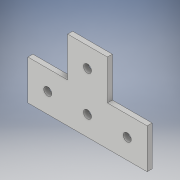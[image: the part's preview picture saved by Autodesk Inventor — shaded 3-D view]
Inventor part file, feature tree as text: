
AUTODESK INVENTOR PART (.ipt)
format: ipt  version: 2018 (Build 220112000, 112)  size: 110,592 bytes
history: native  units: in
note: dims shown in document units (in); Inventor stores cm internally (conversion verified against a paired STEP export)
features: extrude x1, sketch x1
ambient origin geometry x8: Origin, YZ Plane, XZ Plane, XY Plane, X Axis, Y Axis, Z Axis, Center Point
bodies: Solid1 (feature_tree)
feature tree (2):
  extrude  "Extrusion1"  Depth=1.0in
  sketch  "Sketch1"  dims[d0=1.0in d1=1.0in d2=1.0in d3=1.0in d4=1.0in d5=1.0in d6=0.5in d7=1.0in d8=1.0in d9=0.2031in d10=0.125in d11=0.0in]
